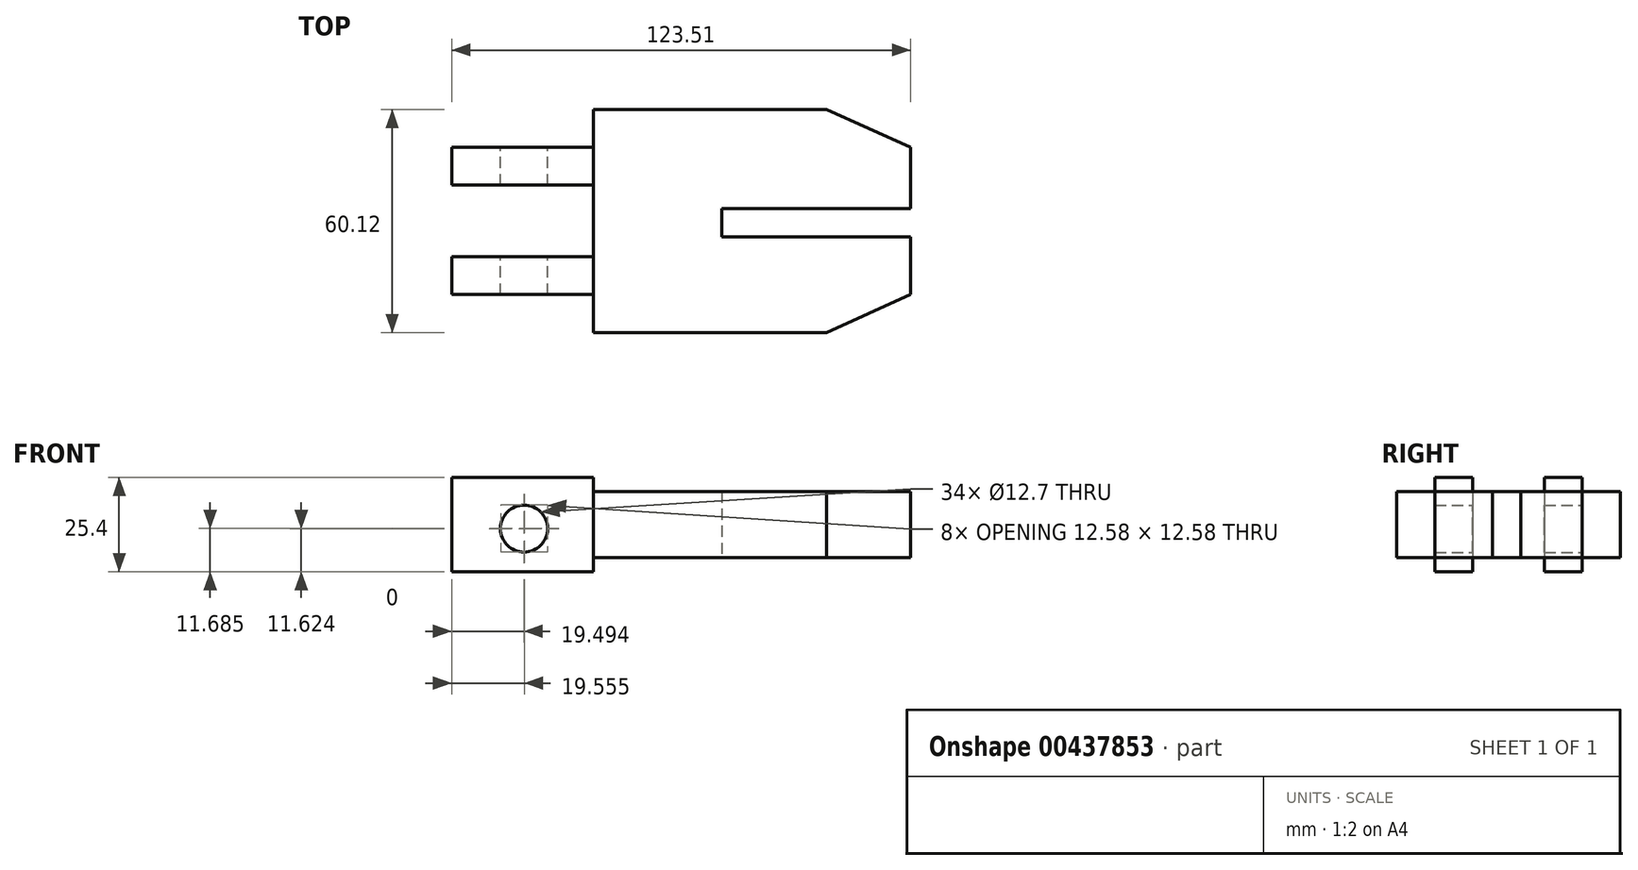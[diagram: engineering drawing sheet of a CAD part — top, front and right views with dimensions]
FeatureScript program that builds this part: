
annotation { "Feature Type Name" : "Feature", "Feature Type Description" : "" }
export const myFeature = defineFeature(function(context is Context, id is Id, definition is map)
    precondition{}
    {
        {
            var Q0;
            Q0=qCreatedBy(makeId("Top.planeOp"),FACE);
            var sketch = newSketch(context, id + "F0", { "sketchPlane" : qUnion([Q0])});
            skLineSegment(sketch, "E0", {"start": v(92, -31.9) * mm, "end": v(92, 7.72) * mm});
            skLineSegment(sketch, "E1", {"start": v(6.6, 7.72) * mm, "end": v(-31.5, 7.72) * mm});
            skLineSegment(sketch, "E2", {"start": v(-31.5, 7.72) * mm, "end": v(-31.5, -2.44) * mm});
            skLineSegment(sketch, "E3", {"start": v(-31.5, -2.44) * mm, "end": v(-12.45, -2.44) * mm});
            skLineSegment(sketch, "E4", {"start": v(-12.45, -2.44) * mm, "end": v(6.6, -2.44) * mm});
            skLineSegment(sketch, "E5", {"start": v(6.6, -2.44) * mm, "end": v(6.6, -21.75) * mm});
            skLineSegment(sketch, "E6", {"start": v(6.6, -21.75) * mm, "end": v(-31.5, -21.75) * mm});
            skLineSegment(sketch, "E7", {"start": v(-31.5, -21.75) * mm, "end": v(-31.5, -31.9) * mm});
            skLineSegment(sketch, "E8", {"start": v(-31.5, -31.9) * mm, "end": v(6.6, -31.9) * mm});
            skLineSegment(sketch, "E9", {"start": v(92, 7.72) * mm, "end": v(69.35, 17.96) * mm});
            skLineSegment(sketch, "E10", {"start": v(69.35, 17.96) * mm, "end": v(6.6, 17.96) * mm});
            skLineSegment(sketch, "E11", {"start": v(6.6, 17.96) * mm, "end": v(6.6, 7.72) * mm});
            skLineSegment(sketch, "E12", {"start": v(92, -31.9) * mm, "end": v(69.35, -42.16) * mm});
            skLineSegment(sketch, "E13", {"start": v(69.35, -42.16) * mm, "end": v(6.6, -42.16) * mm});
            skLineSegment(sketch, "E14", {"start": v(6.6, -42.16) * mm, "end": v(6.6, -31.9) * mm});
            skLineSegment(sketch, "E15", {"start": v(41.23, -12.58) * mm, "end": v(41.23, -16.4) * mm});
            skLineSegment(sketch, "E16", {"start": v(41.23, -16.4) * mm, "end": v(92, -16.4) * mm});
            skLineSegment(sketch, "E17", {"start": v(92, -8.77) * mm, "end": v(41.23, -8.77) * mm});
            skLineSegment(sketch, "E18", {"start": v(41.23, -8.77) * mm, "end": v(41.23, -12.58) * mm});
            skSolve(sketch);
        }
        {
            var Q0;
            Q0=makeQuery(id+"F0.imprint","IMPRINT",FACE,{"disambiguationData":[TD([[makeQuery(id+"F0.imprint","IMPRINT",EDGE,{"derivedFrom":sQuery(id+"F0.wireOp",EDGE,"E1")}),1.0]])]});
            extrude(context, id + "F1", {"entities" : qUnion([Q0]), "depth" : 25.4 * mm});
        }
        {
            var Q0;
            Q0=makeQuery(id+"F1.opExtrude","SWEPT_FACE",FACE,{"disambiguationData":[OSD([sQuery(id+"F0.wireOp",EDGE,"E1")])]});
            var sketch = newSketch(context, id + "F2", { "sketchPlane" : qUnion([Q0])});
            skPoint(sketch, "E19", {"position": v(12, 11.62) * mm});
            skSolve(sketch);
        }
        {
            var Q0;
            Q0=sQuery(id+"F2.wireOp",VERTEX,"E19");
            var Q1;
            Q1=makeQuery(id+"F1.opExtrude","SWEPT_BODY",BODY,{"disambiguationData":[OSD([sQuery(id+"F0.wireOp",EDGE,"E0"),sQuery(id+"F0.wireOp",EDGE,"E1"),sQuery(id+"F0.wireOp",EDGE,"E2"),sQuery(id+"F0.wireOp",EDGE,"E3"),sQuery(id+"F0.wireOp",EDGE,"E4"),sQuery(id+"F0.wireOp",EDGE,"E5"),sQuery(id+"F0.wireOp",EDGE,"E6"),sQuery(id+"F0.wireOp",EDGE,"E7"),sQuery(id+"F0.wireOp",EDGE,"E8"),sQuery(id+"F0.wireOp",EDGE,"E9"),sQuery(id+"F0.wireOp",EDGE,"E10"),sQuery(id+"F0.wireOp",EDGE,"E11"),sQuery(id+"F0.wireOp",EDGE,"E12"),sQuery(id+"F0.wireOp",EDGE,"E13"),sQuery(id+"F0.wireOp",EDGE,"E14"),sQuery(id+"F0.wireOp",EDGE,"E15"),sQuery(id+"F0.wireOp",EDGE,"E16"),sQuery(id+"F0.wireOp",EDGE,"E17"),sQuery(id+"F0.wireOp",EDGE,"E18")])]});
            hole(context, id + "F3", {"style" : HoleStyle.SIMPLE, "endStyle" : HoleEndStyle.THROUGH, "holeDiameter" : 12.7 * mm, "isTappedThrough" : true, "tappedDepth" : 12.7 * mm, "tapClearance" : 3, "locations" : qUnion([Q0]), "scope" : qUnion([Q1])});
        }
        {
            var Q0;
            Q0=makeQuery(id+"F1.opExtrude","CAP_FACE",FACE,{"disambiguationData":[OSD([sQuery(id+"F0.wireOp",EDGE,"E0"),sQuery(id+"F0.wireOp",EDGE,"E1"),sQuery(id+"F0.wireOp",EDGE,"E2"),sQuery(id+"F0.wireOp",EDGE,"E3"),sQuery(id+"F0.wireOp",EDGE,"E4"),sQuery(id+"F0.wireOp",EDGE,"E5"),sQuery(id+"F0.wireOp",EDGE,"E6"),sQuery(id+"F0.wireOp",EDGE,"E7"),sQuery(id+"F0.wireOp",EDGE,"E8"),sQuery(id+"F0.wireOp",EDGE,"E9"),sQuery(id+"F0.wireOp",EDGE,"E10"),sQuery(id+"F0.wireOp",EDGE,"E11"),sQuery(id+"F0.wireOp",EDGE,"E12"),sQuery(id+"F0.wireOp",EDGE,"E13"),sQuery(id+"F0.wireOp",EDGE,"E14"),sQuery(id+"F0.wireOp",EDGE,"E15"),sQuery(id+"F0.wireOp",EDGE,"E16"),sQuery(id+"F0.wireOp",EDGE,"E17"),sQuery(id+"F0.wireOp",EDGE,"E18")])],"isStart":false});
            var sketch = newSketch(context, id + "F4", { "sketchPlane" : qUnion([Q0])});
            skLineSegment(sketch, "E20.bottom", {"start": v(6.6, 17.96) * mm, "end": v(101.43, 17.96) * mm});
            skLineSegment(sketch, "E20.top", {"start": v(6.6, -50.15) * mm, "end": v(101.43, -50.15) * mm});
            skLineSegment(sketch, "E20.left", {"start": v(6.6, 17.96) * mm, "end": v(6.6, -50.15) * mm});
            skLineSegment(sketch, "E20.right", {"start": v(101.43, 17.96) * mm, "end": v(101.43, -50.15) * mm});
            skSolve(sketch);
        }
        {
            var Q0;
            Q0 = qSketchRegion(id + "F4", true);
            extrude(context, id + "F5", {"entities" : qUnion([Q0]), "operationType" : NewBodyOperationType.REMOVE, "oppositeDirection" : true, "depth" : 3.8 * mm});
        }
        {
            var Q0;
            Q0=makeQuery(id+"F1.opExtrude","CAP_FACE",FACE,{"disambiguationData":[OSD([sQuery(id+"F0.wireOp",EDGE,"E0"),sQuery(id+"F0.wireOp",EDGE,"E1"),sQuery(id+"F0.wireOp",EDGE,"E2"),sQuery(id+"F0.wireOp",EDGE,"E3"),sQuery(id+"F0.wireOp",EDGE,"E4"),sQuery(id+"F0.wireOp",EDGE,"E5"),sQuery(id+"F0.wireOp",EDGE,"E6"),sQuery(id+"F0.wireOp",EDGE,"E7"),sQuery(id+"F0.wireOp",EDGE,"E8"),sQuery(id+"F0.wireOp",EDGE,"E9"),sQuery(id+"F0.wireOp",EDGE,"E10"),sQuery(id+"F0.wireOp",EDGE,"E11"),sQuery(id+"F0.wireOp",EDGE,"E12"),sQuery(id+"F0.wireOp",EDGE,"E13"),sQuery(id+"F0.wireOp",EDGE,"E14"),sQuery(id+"F0.wireOp",EDGE,"E15"),sQuery(id+"F0.wireOp",EDGE,"E16"),sQuery(id+"F0.wireOp",EDGE,"E17"),sQuery(id+"F0.wireOp",EDGE,"E18")])],"isStart":true});
            var sketch = newSketch(context, id + "F6", { "sketchPlane" : qUnion([Q0])});
            skLineSegment(sketch, "E21.bottom", {"start": v(6.6, 42.16) * mm, "end": v(101.22, 42.16) * mm});
            skLineSegment(sketch, "E21.top", {"start": v(6.6, -34.1) * mm, "end": v(101.22, -34.1) * mm});
            skLineSegment(sketch, "E21.left", {"start": v(6.6, 42.16) * mm, "end": v(6.6, -34.1) * mm});
            skLineSegment(sketch, "E21.right", {"start": v(101.22, 42.16) * mm, "end": v(101.22, -34.1) * mm});
            skSolve(sketch);
        }
        {
            var Q0;
            Q0 = qSketchRegion(id + "F6", true);
            extrude(context, id + "F7", {"entities" : qUnion([Q0]), "operationType" : NewBodyOperationType.REMOVE, "oppositeDirection" : true, "depth" : 3.8 * mm});
        }
    });
